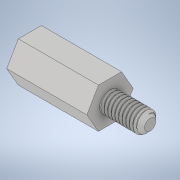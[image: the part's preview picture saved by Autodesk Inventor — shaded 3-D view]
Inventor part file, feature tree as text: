
AUTODESK INVENTOR PART (.ipt)
format: ipt  version: 2021 (Build 250183000, 183)  size: 1,302,016 bytes
history: native  units: in
note: dims shown in document units (in); Inventor stores cm internally (conversion verified against a paired STEP export)
features: sketch x2, chamfer x2, revolve x1, helix x1, other x1, extrude x1
ambient origin geometry x8: Origin, YZ Plane, XZ Plane, XY Plane, X Axis, Y Axis, Z Axis, Center Point
bodies: Solid1 (feature_tree)
feature tree (8):
  sketch  "Sketch3"  dims[d3=0.0806in d33=0.2283in]
  revolve  "Revolution1"  [1 undecoded]
  chamfer  "Fase3"  Distance=0.1969in
  helix  "Coil2"  [1 undecoded]
  chamfer  "Fase4"  Distance=0.0177in Angle=60.0deg
  other  "Spirale3"
  extrude  "Extrusion2"  TaperAngle=60.0deg  [1 undecoded]
  sketch  "Skizze4"  dims[d36=0.1024in d37=0.1969in d38=90.0deg d53=60.0deg d54=0.0177in d55=0.0026in d57=60.0deg d58=0.0394in d59=0.0057in d60=0.1024in d61=90.0deg d62=0.0806in d63=0.0011in d64=-0.0011in d65=0.0177in d66=0.1969in d67=0.3937in d68=0.0in d69=90.0deg d70=90.0deg d71=0.0in d72=0.0in d77=0.0236in d78=0.0787in d79=45.0deg d80=60.0deg d81=0.1181in d82=0.0177in d83=0.0989in d84=0.0096in d85=0.0019in d86=60.0deg d87=0.1181in d88=0.0177in d89=0.0989in d90=0.0153in d91=0.0989in d93=0.1181in d94=90.0deg d97=0.3937in d99=0.0in d100=0.0177in d101=0.2756in d102=6.2992in d103=0.0in d104=90.0deg d105=90.0deg d106=0.0in d107=0.0in d108=0.0157in d109=0.0787in d110=45.0deg d111=0.1969in d112=0.1969in d113=0.1969in d114=0.3937in d115=0.0in]
note: 3 required parameter values undecoded (feature->parameter linkage not recoverable at this tier; creation-order binding heuristic only, values carry confidence <= 0.55)